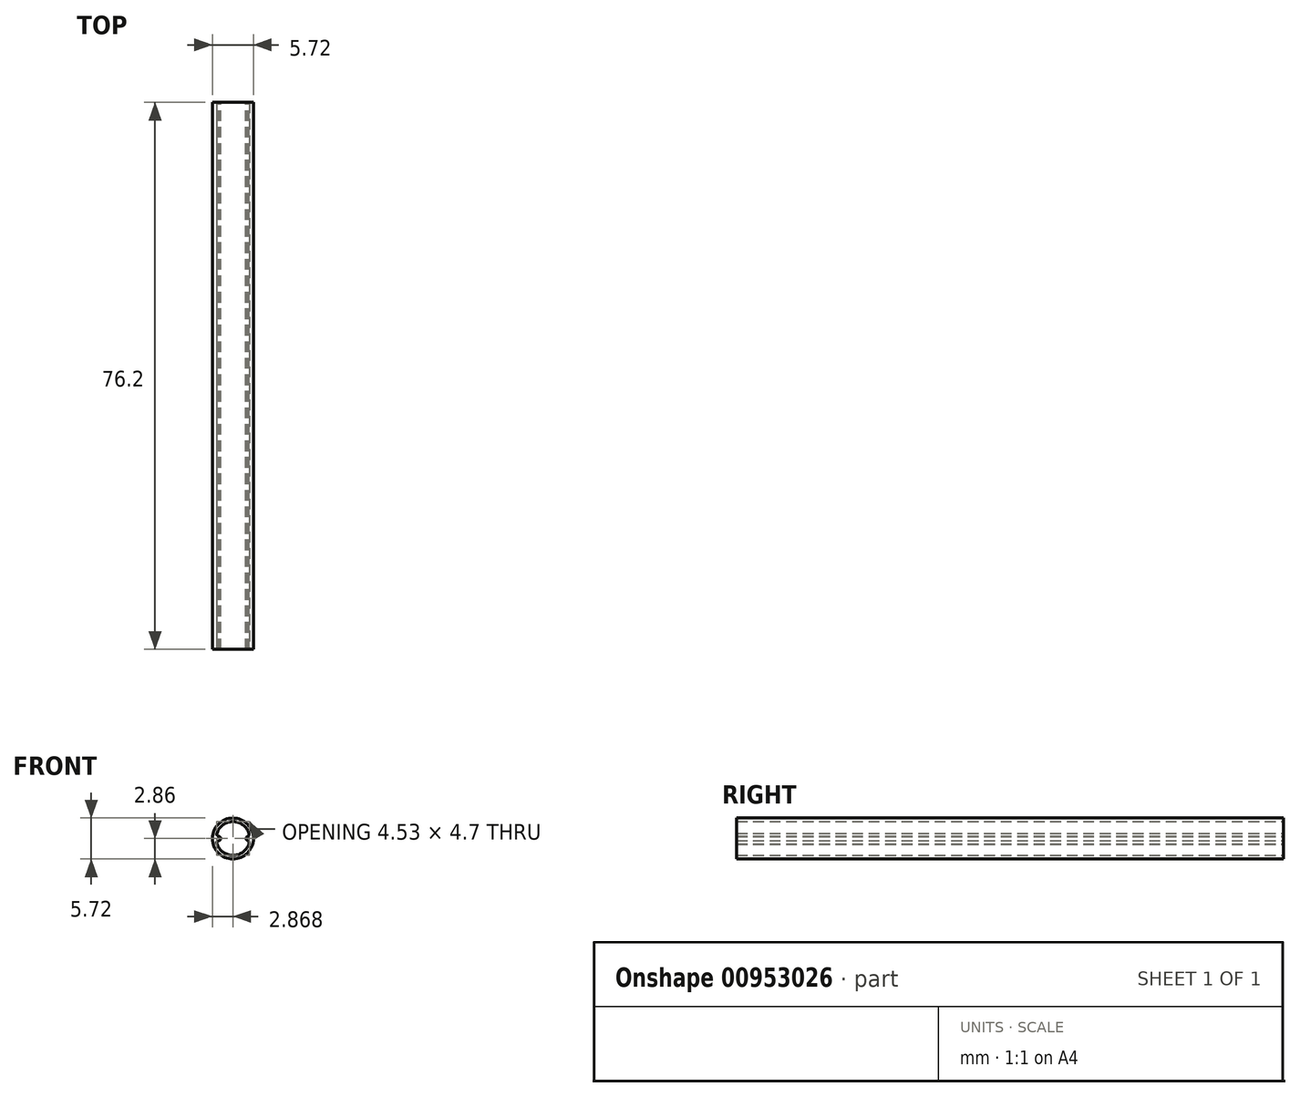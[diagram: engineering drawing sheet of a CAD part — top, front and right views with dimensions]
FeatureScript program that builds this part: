
annotation { "Feature Type Name" : "Feature", "Feature Type Description" : "" }
export const myFeature = defineFeature(function(context is Context, id is Id, definition is map)
    precondition{}
    {
        {
            var Q0;
            Q0=qCreatedBy(makeId("Front.planeOp"),FACE);
            var sketch = newSketch(context, id + "F0", { "sketchPlane" : qUnion([Q0])});
            skCircle(sketch, "E0", {"center": v(0, 0) * mm, "radius": 2.86 * mm});
            skArc(sketch, "E1", {"start": v(-2.22, -0.76) * mm, "mid": v(-0.01, -2.35) * mm, "end": v(2.22, -0.78) * mm});
            skEllipticalArc(sketch, "E2", {});
            skFitSpline(sketch, "E3", {"points": [v(-2.23, 0.74) * mm, v(-2.23, 0.48) * mm, v(-2, 0.33) * mm], "startDerivative": vector(-0.17, -1.06) * mm, "endDerivative": vector(0.78, -0.14) * mm});
            skFitSpline(sketch, "E4", {"points": [v(-1.96, -0.31) * mm, v(-2.21, -0.4) * mm, v(-2.22, -0.76) * mm], "startDerivative": vector(-0.7, -0.29) * mm, "endDerivative": vector(0.22, -0.98) * mm});
            skEllipticalArc(sketch, "E5", {});
            skPoint(sketch, "E5.centerSnap0", {"position": v(2.35, 0) * mm});
            skArc(sketch, "E6.trimOffspring", {"start": v(2.23, 0.74) * mm, "mid": v(0, 2.35) * mm, "end": v(-2.23, 0.74) * mm});
            skFitSpline(sketch, "E7", {"points": [v(2.23, 0.74) * mm, v(2.26, 0.47) * mm, v(2.07, 0.3) * mm], "startDerivative": vector(0.18, -0.56) * mm, "endDerivative": vector(-0.72, -0.18) * mm});
            skFitSpline(sketch, "E8", {"points": [v(2.22, -0.78) * mm, v(2.26, -0.44) * mm, v(2.05, -0.3) * mm], "startDerivative": vector(0.2, 1.06) * mm, "endDerivative": vector(-0.73, 0.54) * mm});
            const initialGuessF0  = {"E2": [-0.0022120324167538593, 0, 1, 0, 0.0005334000000000001, 0.0003556, 5.21196438342495, 1.1767650168940162], "E5": [0.002349495893537985, 4.3927494971551025e-06, -1, 0, 0.0005334000000000001, 0.0003556, 5.266476213945207, 0.9799257492594527]};
            skSetInitialGuess(sketch, initialGuessF0);
            skSolve(sketch);
        }
        {
            var Q0;
            Q0=makeQuery(id+"F0.imprint","IMPRINT",FACE,{"disambiguationData":[TD([[makeQuery(id+"F0.imprint","IMPRINT",EDGE,{"derivedFrom":sQuery(id+"F0.wireOp",EDGE,"E0")}),1.0]])]});
            extrude(context, id + "F1", {"entities" : qUnion([Q0]), "depth" : 76.2 * mm, "offsetDistance" : 25.4 * mm});
        }
    });
